# Revit family: Data_Device-Network-Leviton-Patch_Panel-Angled
name_source: partatom
category: Data Devices
units: mm (PartAtom-declared; Revit-internal decimal feet)

## family parameters
Cut with Voids When Loaded = No
Host = Face
Maintain Annotation Orientation = Yes
OmniClass Number = 23.85.50.17
OmniClass Title = Communication and Data Processing Equipment
Part Type = Normal
Room Calculation Point = No
Round Connector Dimension = Use Diameter
Shared = Yes

## types (7) — shared parameters
Annotation Symbol is Visible = Yes
Assembly Code = D5030600
Date Last Modified = September 06, 2023
Default Elevation = 24 "
Die Cast = No
Equipment Abbreviation = QPPA
Family Version = 1.0.2
Manufacturer = Leviton
Model Disclaimer = http://www.leviton.com
URL = http://www.leviton.com
z Depth = 0.0598 "
z Offset 1 = 0.0598 "
z Offset 2 = 0.5 "
zero-valued in all types: z Void Offset

## per-type parameters (varying)
| type | Description | Has ID Windows | Part Description | Product Documentation Link | Rack Spaces RU | Shielded | z 1 Y Offset 1 | z 1 Y Offset 2 | z 1 Y Offset 3 | z 1 Y Offset 4 | z 1 Y Offset 5 | z 1RU with Lens | z 1RU with Screen | z 2RU with Lens | z 2RU with Screen | z Has 24 Ports | z Has 48 Ports | z Has 48 Ports 1RU | z Height | z Is Visible 2RU | z Leviton Type |
| 1RU, 24-Port | Angled QuickPort Patch Panel, 24-port, 1RU | No | Angled QuickPort Patch Panel, 24-port, 1RU | Leviton_49256-Hxx_49256-Dxx_49256-Lxx_Angled_QuickPort_Patch_Panels.pdf | 1 | No | 0.6 " | 18 " | 18 " | 0.16 " | 0.45 " | No | Yes | No | No | Yes | No | No | 1.725 " | No | 110 |
| 2RU, 48-Port, Shielded | ATLAS-X1 Shielded Angled QuickPort Patch Panel, 48 ports, 2RU, black | No | ATLAS-X1 Shielded Angled QuickPort Patch Panel, 48 ports, 2RU, black | Leviton_4S256-Sxx_AtlasX1_Shielded_Angled_QuickPort_Patch_Panels.pdf | 2 | Yes | 0.639 " | 2.307 " | 2.307 " | 18 " | 0.45 " | No | No | No | Yes | No | Yes | No | 3.475 " | Yes | 221 |
| 2RU, 48-Port | Angled QuickPort Patch Panel, 48-port, 2RU | No | Angled QuickPort Patch Panel, 48-port, 2RU | Leviton_49256-Hxx_49256-Dxx_49256-Lxx_Angled_QuickPort_Patch_Panels.pdf | 2 | No | 0.639 " | 2.307 " | 2.307 " | 18 " | 0.45 " | No | No | No | Yes | No | Yes | No | 3.475 " | Yes | 220 |
| 1RU, 48-Port, High Density | Angled QuickPort High-Density Patch Panel, 48-port, 1RU | No | Angled QuickPort High-Density Patch Panel, 48-port, 1RU | https://www.leviton.com | 1 | No | 0.2059 " | 1.0191 " | 1.0191 " | 18 " | 0.45 " | No | No | No | No | No | No | Yes | 1.725 " | No | 120 |
| 1RU, 24-Port, Shielded | ATLAS-X1 Shielded Angled QuickPort Patch Panel, 24 ports, 1RU, black | No | ATLAS-X1 Shielded Angled QuickPort Patch Panel, 24 ports, 1RU, black | Leviton_4S256-Sxx_AtlasX1_Shielded_Angled_QuickPort_Patch_Panels.pdf | 1 | Yes | 0.6 " | 18 " | 18 " | 0.16 " | 0.45 " | No | Yes | No | No | Yes | No | No | 1.725 " | No | 111 |
| 1RU, 24-Port, with Lens | Angled QuickPort Patch Panel, 24-port, 1RU, with Magnifying Lens | Yes | Angled QuickPort Patch Panel, 24-port, 1RU, with Magnifying Lens | Leviton_49256-Hxx_49256-Dxx_49256-Lxx_Angled_QuickPort_Patch_Panels.pdf | 1 | No | 0.6 " | 18 " | 18 " | 0.16 " | 0.45 " | Yes | No | No | No | Yes | No | No | 1.725 " | No | 112 |
| 2RU, 48-Port, with Lens | Angled QuickPort Patch Panel, 48-port, 2RU, with Mangnifying Lens | Yes | Angled QuickPort Patch Panel, 48-port, 2RU, with Mangnifying Lens | Leviton_49256-Hxx_49256-Dxx_49256-Lxx_Angled_QuickPort_Patch_Panels.pdf | 2 | No | 0.639 " | 2.307 " | 2.307 " | 18 " | 1.5 " | No | No | Yes | No | No | Yes | No | 3.475 " | Yes | 222 |

## geometry (parser evidence)
native form markers: Blend x6, Sweep x7
no freeform markers — native parametric forms only
